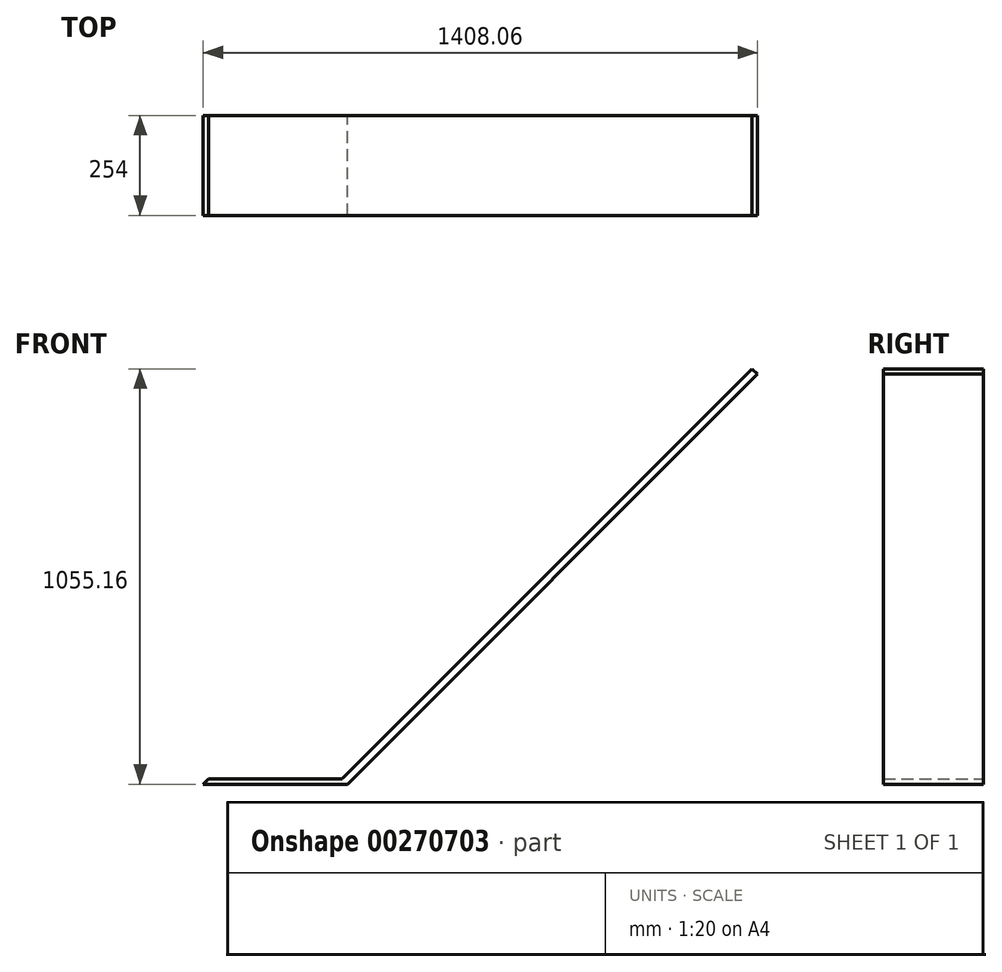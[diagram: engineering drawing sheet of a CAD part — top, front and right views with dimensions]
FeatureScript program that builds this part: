
annotation { "Feature Type Name" : "Feature", "Feature Type Description" : "" }
export const myFeature = defineFeature(function(context is Context, id is Id, definition is map)
    precondition{}
    {
        {
            var Q0;
            Q0=qCreatedBy(makeId("Front.planeOp"),FACE);
            var sketch = newSketch(context, id + "F0", { "sketchPlane" : qUnion([Q0])});
            skLineSegment(sketch, "E0", {"start": v(0, 0) * mm, "end": v(1041.73, 1041.69) * mm});
            skLineSegment(sketch, "E1", {"start": v(1041.73, 1041.69) * mm, "end": v(1055.2, 1028.22) * mm});
            skLineSegment(sketch, "E2", {"start": v(1055.2, 1028.22) * mm, "end": v(13.47, -13.47) * mm});
            skLineSegment(sketch, "E3", {"start": v(13.47, -13.47) * mm, "end": v(-354.65, -13.47) * mm});
            skLineSegment(sketch, "E4", {"start": v(-354.67, 0) * mm, "end": v(0, 0) * mm});
            skLineSegment(sketch, "E5", {"start": v(-354.65, -13.47) * mm, "end": v(-354.67, 0) * mm});
            skSolve(sketch);
        }
        {
            var Q0;
            Q0 = qSketchRegion(id + "F0", true);
            extrude(context, id + "F1", {"entities" : qUnion([Q0]), "depth" : 254 * mm});
        }
        {
            var Q0;
            Q0=makeQuery(id+"F1.opExtrude","SWEPT_EDGE",EDGE,{"disambiguationData":[OSD([sQuery(id+"F0.wireOp",EDGE,"E4"),sQuery(id+"F0.wireOp",EDGE,"E5")])]});
            chamfer(context, id + "F2", {"entities" : qUnion([Q0]), "width" : 15.24 * mm, "tangentPropagation" : true});
        }
        {
            var Q0;
            Q0=makeQuery(id+"F1.opExtrude","SWEPT_EDGE",EDGE,{"disambiguationData":[OSD([sQuery(id+"F0.wireOp",EDGE,"E0"),sQuery(id+"F0.wireOp",EDGE,"E4")])]});
            fillet(context, id + "F3", {"entities" : qUnion([Q0]), "radius" : 5.08 * mm, "tangentPropagation" : true, "allowEdgeOverflow" : false});
        }
    });
